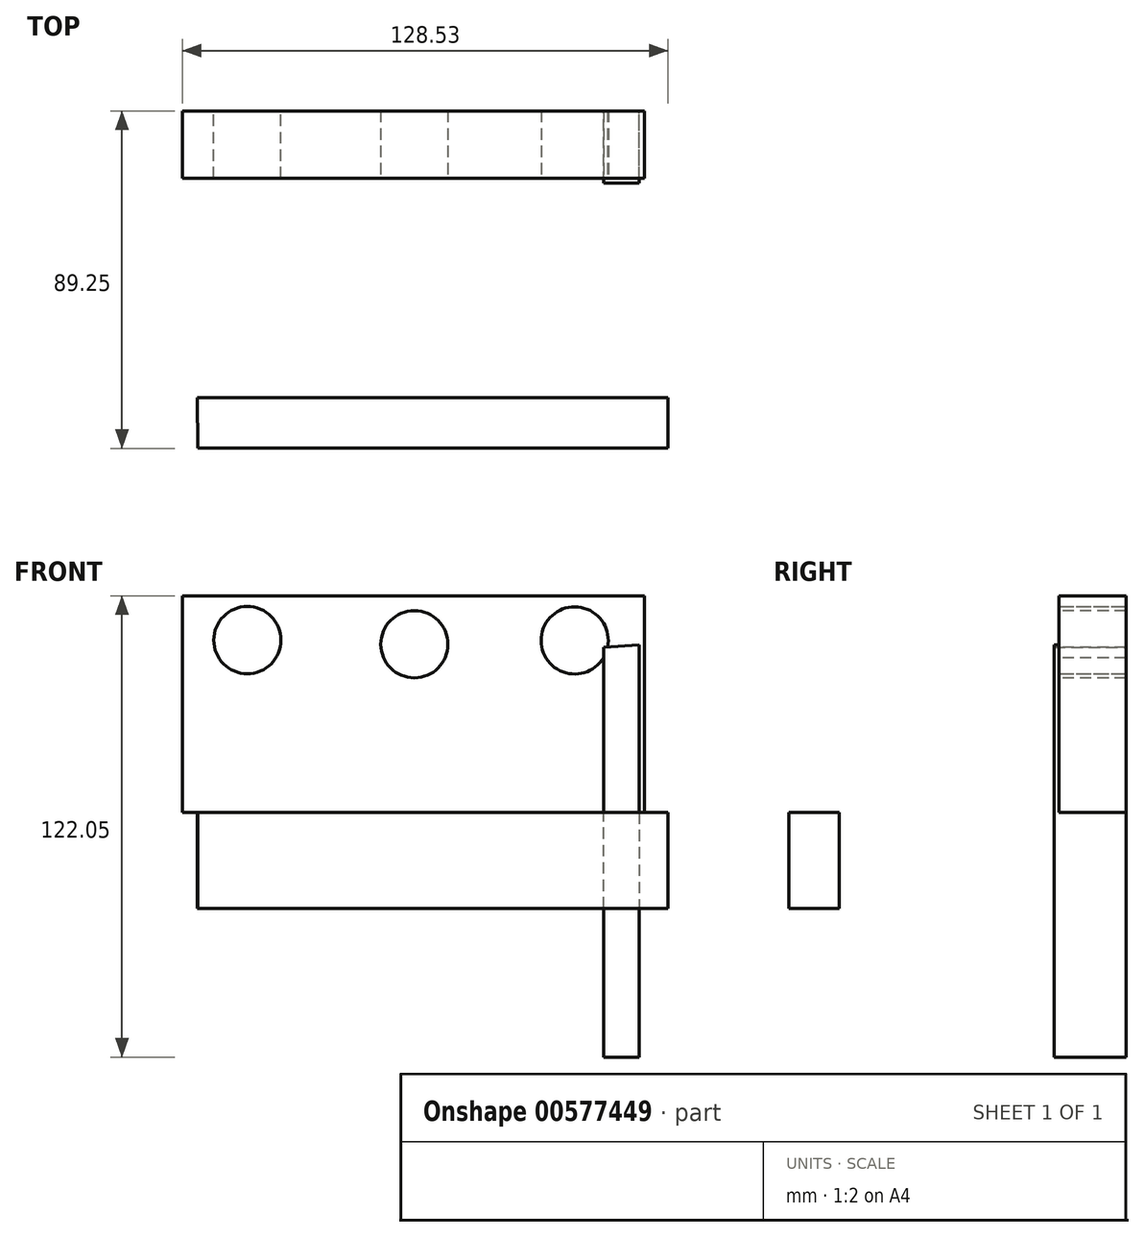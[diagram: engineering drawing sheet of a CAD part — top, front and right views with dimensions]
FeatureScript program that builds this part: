
annotation { "Feature Type Name" : "Feature", "Feature Type Description" : "" }
export const myFeature = defineFeature(function(context is Context, id is Id, definition is map)
    precondition{}
    {
        {
            var Q0;
            Q0=qCreatedBy(makeId("Front.planeOp"),FACE);
            var sketch = newSketch(context, id + "F0", { "sketchPlane" : qUnion([Q0])});
            skLineSegment(sketch, "E0", {"start": v(-61.39, 0) * mm, "end": v(-61.39, 57.32) * mm});
            skLineSegment(sketch, "E1", {"start": v(-61.39, 57.32) * mm, "end": v(60.9, 57.32) * mm});
            skLineSegment(sketch, "E2", {"start": v(60.9, 57.32) * mm, "end": v(60.9, 0) * mm});
            skLineSegment(sketch, "E3", {"start": v(-61.39, 0) * mm, "end": v(60.9, 0) * mm});
            skSolve(sketch);
        }
        {
            var Q0;
            Q0=makeQuery(id+"F0.imprint","IMPRINT",FACE,{"disambiguationData":[TD([[makeQuery(id+"F0.imprint","IMPRINT",EDGE,{"derivedFrom":sQuery(id+"F0.wireOp",EDGE,"E0")}),-1.0]])]});
            var sketch = newSketch(context, id + "F1", { "sketchPlane" : qUnion([Q0])});
            skLineSegment(sketch, "E4", {"start": v(-60.64, 56.8) * mm, "end": v(-60.64, 0) * mm});
            skLineSegment(sketch, "E5", {"start": v(-60.64, 0) * mm, "end": v(60.73, 0) * mm});
            skLineSegment(sketch, "E6", {"start": v(60.73, 0) * mm, "end": v(60.73, 56.29) * mm});
            skLineSegment(sketch, "E7", {"start": v(60.73, 56.29) * mm, "end": v(-60.64, 56.8) * mm});
            skSolve(sketch);
        }
        {
            var Q0;
            Q0=makeQuery(id+"F1.imprint","IMPRINT",FACE,{"disambiguationData":[TD([[makeQuery(id+"F1.imprint","IMPRINT",EDGE,{"derivedFrom":sQuery(id+"F1.wireOp",EDGE,"E4")}),1.0]])]});
            extrude(context, id + "F2", {"entities" : qUnion([Q0]), "depth" : 17.78 * mm, "offsetDistance" : 25.4 * mm});
        }
        {
            var Q0;
            Q0=makeQuery(id+"F0.imprint","IMPRINT",FACE,{"disambiguationData":[TD([[makeQuery(id+"F0.imprint","IMPRINT",EDGE,{"derivedFrom":sQuery(id+"F0.wireOp",EDGE,"E0")}),-1.0]])]});
            extrude(context, id + "F3", {"entities" : qUnion([Q0]), "operationType" : NewBodyOperationType.ADD, "depth" : 17.78 * mm, "offsetDistance" : 25.4 * mm});
        }
        {
            var Q0;
            Q0=qCreatedBy(makeId("Front.planeOp"),FACE);
            var sketch = newSketch(context, id + "F4", { "sketchPlane" : qUnion([Q0])});
            skPoint(sketch, "E8", {"position": v(-44.21, 45.58) * mm});
            skPoint(sketch, "E9", {"position": v(50.12, 45.58) * mm});
            skSolve(sketch);
        }
        {
            var Q0;
            Q0=sQuery(id+"F4.wireOp",VERTEX,"E8");
            var Q1;
            Q1=makeQuery(id+"F2.opExtrude","SWEPT_BODY",BODY,{"disambiguationData":[OSD([sQuery(id+"F1.wireOp",EDGE,"E4"),sQuery(id+"F1.wireOp",EDGE,"E5"),sQuery(id+"F1.wireOp",EDGE,"E6"),sQuery(id+"F1.wireOp",EDGE,"E7")])]});
            hole(context, id + "F5", {"style" : HoleStyle.SIMPLE, "endStyle" : HoleEndStyle.THROUGH, "oppositeDirection" : true, "holeDiameter" : 17.78 * mm, "isTappedThrough" : true, "tappedDepth" : 12.7 * mm, "tapClearance" : 3, "locations" : qUnion([Q0]), "scope" : qUnion([Q1])});
        }
        {
            var Q0;
            Q0=makeQuery(id+"F3.boolean.opBoolean","MERGE",FACE,{"derivedFrom":[makeQuery(id+"F2.opExtrude","CAP_FACE",FACE,{"disambiguationData":[OSD([sQuery(id+"F1.wireOp",EDGE,"E4"),sQuery(id+"F1.wireOp",EDGE,"E5"),sQuery(id+"F1.wireOp",EDGE,"E6"),sQuery(id+"F1.wireOp",EDGE,"E7")])],"isStart":false}),makeQuery(id+"F3.opExtrude","CAP_FACE",FACE,{"disambiguationData":[OSD([sQuery(id+"F0.wireOp",EDGE,"E0"),sQuery(id+"F0.wireOp",EDGE,"E1"),sQuery(id+"F0.wireOp",EDGE,"E2"),sQuery(id+"F0.wireOp",EDGE,"E3")])],"isStart":false})]});
            var sketch = newSketch(context, id + "F6", { "sketchPlane" : qUnion([Q0])});
            skSolve(sketch);
        }
        {
            var Q0;
            {var subQ4=sQuery(id+"F0.wireOp",EDGE,"E0");Q0=makeQuery(id+"F6.imprint","IMPRINT",FACE,{"disambiguationData":[TD([[makeQuery(id+"F6.imprint","IMPRINT",EDGE,{"derivedFrom":makeQuery(id+"F3.opExtrude","CAP_EDGE",EDGE,{"disambiguationData":[OSD([subQ4])],"isStart":false})}),-1.0]])]});}
            var sketch = newSketch(context, id + "F7", { "sketchPlane" : qUnion([Q0])});
            skPoint(sketch, "E10", {"position": v(45.94, 44.49) * mm});
            skPoint(sketch, "E11", {"position": v(0, 44.49) * mm});
            skPoint(sketch, "E12", {"position": v(45.94, 13.74) * mm});
            skPoint(sketch, "E13", {"position": v(0, 14.15) * mm});
            skSolve(sketch);
        }
        {
            var Q0;
            Q0=sQuery(id+"F7.wireOp",VERTEX,"E11");
            var Q1;
            Q1=makeQuery(id+"F2.opExtrude","SWEPT_BODY",BODY,{"disambiguationData":[OSD([sQuery(id+"F1.wireOp",EDGE,"E4"),sQuery(id+"F1.wireOp",EDGE,"E5"),sQuery(id+"F1.wireOp",EDGE,"E6"),sQuery(id+"F1.wireOp",EDGE,"E7")])]});
            hole(context, id + "F8", {"style" : HoleStyle.SIMPLE, "endStyle" : HoleEndStyle.THROUGH, "holeDiameter" : 17.78 * mm, "isTappedThrough" : true, "tappedDepth" : 12.7 * mm, "tapClearance" : 3, "locations" : qUnion([Q0]), "scope" : qUnion([Q1])});
        }
        {
            var Q0;
            {var subQ4=sQuery(id+"F0.wireOp",EDGE,"E0");Q0=makeQuery(id+"F6.imprint","IMPRINT",FACE,{"disambiguationData":[TD([[makeQuery(id+"F6.imprint","IMPRINT",EDGE,{"derivedFrom":makeQuery(id+"F3.opExtrude","CAP_EDGE",EDGE,{"disambiguationData":[OSD([subQ4])],"isStart":false})}),-1.0]])]});}
            var sketch = newSketch(context, id + "F9", { "sketchPlane" : qUnion([Q0])});
            skPoint(sketch, "E14", {"position": v(42.43, 45.5) * mm});
            skSolve(sketch);
        }
        {
            var Q0;
            Q0=sQuery(id+"F9.wireOp",VERTEX,"E14");
            var Q1;
            Q1=makeQuery(id+"F2.opExtrude","SWEPT_BODY",BODY,{"disambiguationData":[OSD([sQuery(id+"F1.wireOp",EDGE,"E4"),sQuery(id+"F1.wireOp",EDGE,"E5"),sQuery(id+"F1.wireOp",EDGE,"E6"),sQuery(id+"F1.wireOp",EDGE,"E7")])]});
            hole(context, id + "F10", {"style" : HoleStyle.SIMPLE, "endStyle" : HoleEndStyle.THROUGH, "holeDiameter" : 17.78 * mm, "isTappedThrough" : true, "tappedDepth" : 12.7 * mm, "tapClearance" : 3, "locations" : qUnion([Q0]), "scope" : qUnion([Q1])});
        }
        {
            var Q0;
            Q0=qCreatedBy(makeId("Top.planeOp"),FACE);
            var sketch = newSketch(context, id + "F11", { "sketchPlane" : qUnion([Q0])});
            skLineSegment(sketch, "E15", {"start": v(-57.49, -75.87) * mm, "end": v(67.14, -75.87) * mm});
            skLineSegment(sketch, "E16", {"start": v(67.14, -75.87) * mm, "end": v(67.14, -89.25) * mm});
            skLineSegment(sketch, "E17", {"start": v(67.14, -89.25) * mm, "end": v(-57.34, -89.25) * mm});
            skLineSegment(sketch, "E18", {"start": v(-57.34, -89.25) * mm, "end": v(-57.49, -75.87) * mm});
            skSolve(sketch);
        }
        {
            var Q0;
            Q0=makeQuery(id+"F11.imprint","IMPRINT",FACE,{"disambiguationData":[TD([[makeQuery(id+"F11.imprint","IMPRINT",EDGE,{"derivedFrom":sQuery(id+"F11.wireOp",EDGE,"E15")}),-1.0]])]});
            extrude(context, id + "F12", {"entities" : qUnion([Q0]), "oppositeDirection" : true, "depth" : 25.4 * mm, "offsetDistance" : 25.4 * mm});
        }
        {
            var Q0;
            Q0=qCreatedBy(makeId("Front.planeOp"),FACE);
            var sketch = newSketch(context, id + "F13", { "sketchPlane" : qUnion([Q0])});
            skLineSegment(sketch, "E19", {"start": v(59.56, 44.36) * mm, "end": v(59.56, -64.73) * mm});
            skLineSegment(sketch, "E20", {"start": v(59.56, -64.73) * mm, "end": v(50.06, -64.73) * mm});
            skLineSegment(sketch, "E21", {"start": v(50.06, -64.73) * mm, "end": v(50.06, 43.63) * mm});
            skLineSegment(sketch, "E22", {"start": v(50.06, 43.63) * mm, "end": v(59.56, 44.36) * mm});
            skSolve(sketch);
        }
        {
            var Q0;
            Q0=makeQuery(id+"F13.imprint","IMPRINT",FACE,{"disambiguationData":[TD([[makeQuery(id+"F13.imprint","IMPRINT",EDGE,{"derivedFrom":sQuery(id+"F13.wireOp",EDGE,"E19")}),-1.0]])]});
            extrude(context, id + "F14", {"entities" : qUnion([Q0]), "operationType" : NewBodyOperationType.ADD, "depth" : 19.05 * mm, "offsetDistance" : 25.4 * mm});
        }
    });
